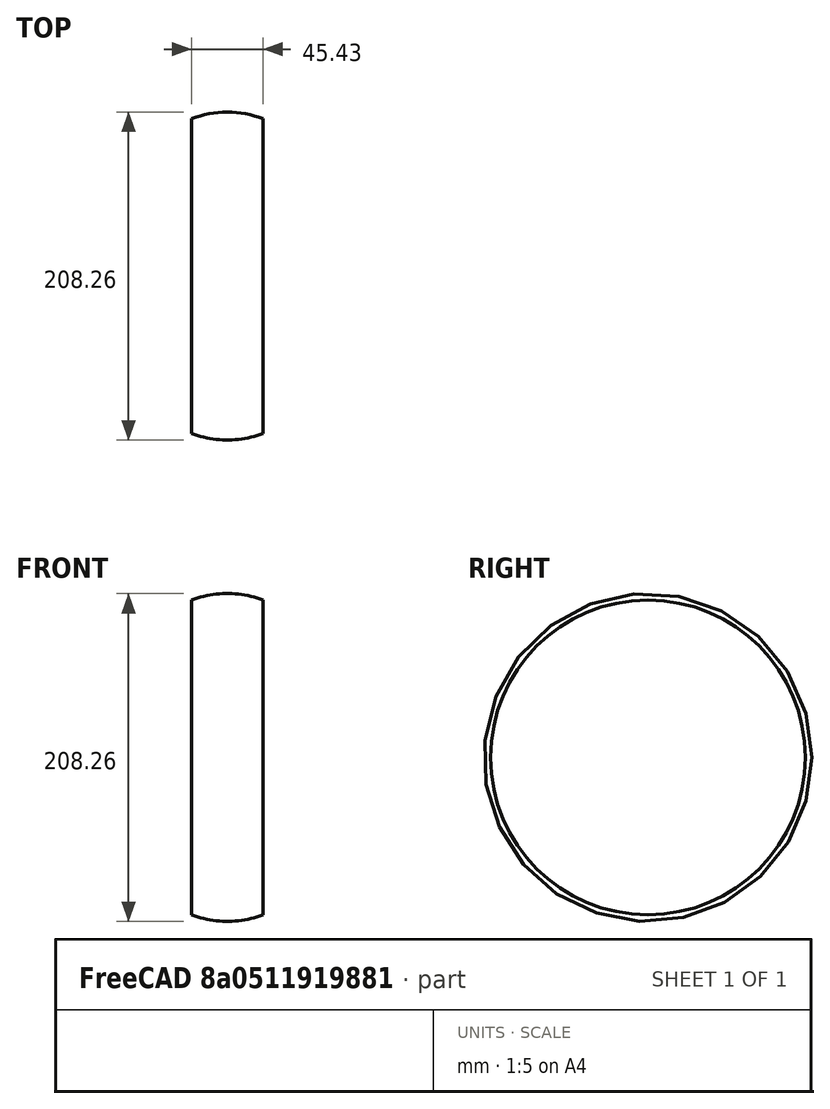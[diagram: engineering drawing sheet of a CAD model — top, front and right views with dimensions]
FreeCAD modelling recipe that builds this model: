
FCSTD DOCUMENT
Label: gyuru_volume_kozep
objects: Sketcher::SketchObject×1, Part::Revolution×1
note: 2 computed .brp shape members not serialized (recipe doc carries the construction recipe); baked Part::Feature solids carry a one-line shape summary decoded from their .brp

FEATURE [Sketcher::SketchObject] Sketch
  sketch-geometry (4):
    g0: ArcOfCircle CenterX=25 CenterY=40.327 CenterZ=0 NormalX=0 NormalY=0 NormalZ=1 Radius=63.8 StartAngle=1.20686 EndAngle=1.93482
    g1: LineSegment StartX=47.71 StartY=99.9483 StartZ=0 EndX=47.71 EndY=0 EndZ=0
    g2: LineSegment StartX=2.285 StartY=99.9464 StartZ=0 EndX=2.285 EndY=0 EndZ=0
    g3: LineSegment [constr] StartX=12.4448 StartY=104.127 StartZ=0 EndX=46.8726 EndY=104.127 EndZ=0
  constraints (13):
    c: Radius(g0) = 63.8
    c: DistanceX(g0) = 25
    c: DistanceX(g0) = 2.285
    c: DistanceX(g0) = 47.71
    c: Coincident(g1,g0)
    c: PointOnObject(g1,g-1)
    c: Vertical(g1)
    c: Coincident(g2,g0)
    c: PointOnObject(g2,g-1)
    c: Vertical(g2)
    c: Horizontal(g3)
    c: DistanceY(g3) = 104.127
    c: Tangent(g0,g3)
FEATURE [Part::Revolution] Revolve
  Angle = 360
  Axis = (1,0,0)
  Base = (0,0,0)
  Source = -> Sketch
